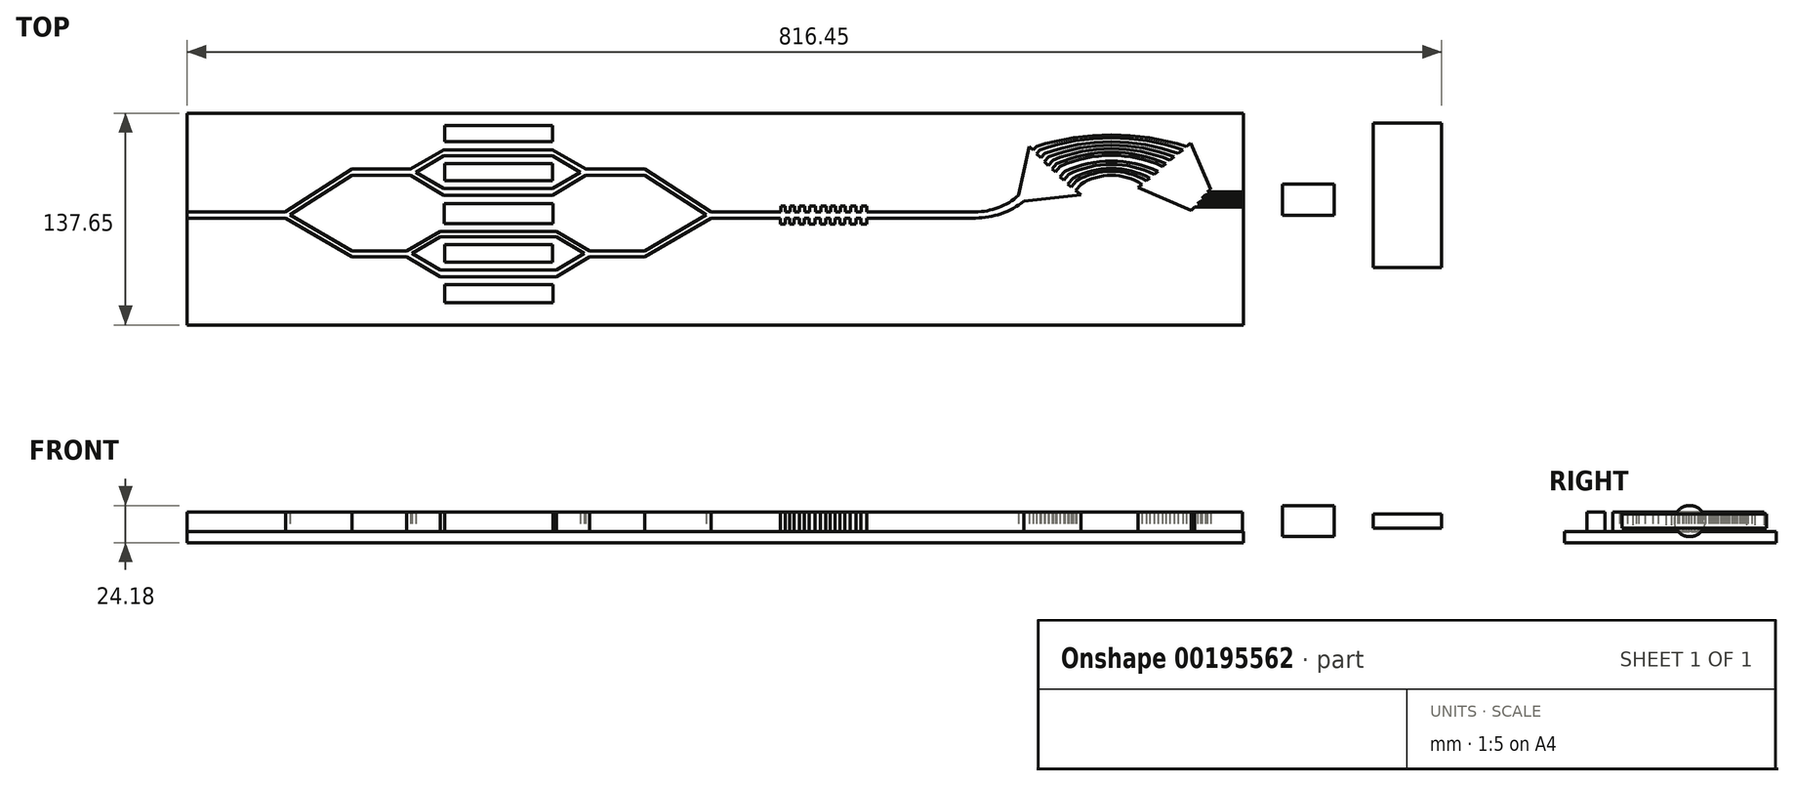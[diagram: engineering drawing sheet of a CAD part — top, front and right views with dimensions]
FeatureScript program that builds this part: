
annotation { "Feature Type Name" : "Feature", "Feature Type Description" : "" }
export const myFeature = defineFeature(function(context is Context, id is Id, definition is map)
    precondition{}
    {
        {
            var Q0;
            Q0=qCreatedBy(makeId("Top.planeOp"),FACE);
            var sketch = newSketch(context, id + "F0", { "sketchPlane" : qUnion([Q0])});
            skLineSegment(sketch, "E0.bottom", {"start": v(-202.47, -68.03) * mm, "end": v(484.95, -68.03) * mm});
            skLineSegment(sketch, "E0.top", {"start": v(-202.47, 69.62) * mm, "end": v(484.95, 69.62) * mm});
            skLineSegment(sketch, "E0.left", {"start": v(-202.47, -68.03) * mm, "end": v(-202.47, 69.62) * mm});
            skLineSegment(sketch, "E0.right", {"start": v(484.95, -68.03) * mm, "end": v(484.95, 69.62) * mm});
            skSolve(sketch);
        }
        {
            var Q0;
            Q0=qSketchRegion(id+"F0",true);
            extrude(context, id + "F1", {"entities" : qUnion([Q0]), "depth" : 7.37 * mm});
        }
        {
            var Q0;
            Q0=makeQuery(id+"F1.opExtrude","CAP_FACE",FACE,{"disambiguationData":[OSD([sQuery(id+"F0.wireOp",EDGE,"E0.bottom"),sQuery(id+"F0.wireOp",EDGE,"E0.top"),sQuery(id+"F0.wireOp",EDGE,"E0.left"),sQuery(id+"F0.wireOp",EDGE,"E0.right")])],"isStart":false});
            var sketch = newSketch(context, id + "F2", { "sketchPlane" : qUnion([Q0])});
            skLineSegment(sketch, "E1.bottom", {"start": v(-156.35, 5.45) * mm, "end": v(-138.65, 5.45) * mm});
            skLineSegment(sketch, "E1.top", {"start": v(-156.6, 1.4) * mm, "end": v(-138.42, 1.4) * mm});
            skLineSegment(sketch, "E2", {"start": v(-138.65, 5.45) * mm, "end": v(-95.28, 33.3) * mm});
            skLineSegment(sketch, "E3.MirrorCS", {"start": v(-138.42, 1.4) * mm, "end": v(-95.29, -23.79) * mm});
            skLineSegment(sketch, "E4", {"start": v(-95.29, 29.2) * mm, "end": v(-135.34, 3.48) * mm});
            skLineSegment(sketch, "E5", {"start": v(-95.29, -19.91) * mm, "end": v(-135.34, 3.48) * mm});
            skLineSegment(sketch, "E6", {"start": v(-95.28, 33.3) * mm, "end": v(-57.06, 33.3) * mm});
            skLineSegment(sketch, "E7", {"start": v(-95.29, 29.2) * mm, "end": v(-57.06, 29.2) * mm});
            skLineSegment(sketch, "E8", {"start": v(-95.29, -19.91) * mm, "end": v(-59.46, -19.91) * mm});
            skLineSegment(sketch, "E9", {"start": v(-95.29, -23.79) * mm, "end": v(-59.46, -23.79) * mm});
            skLineSegment(sketch, "E10", {"start": v(-57.06, 33.3) * mm, "end": v(-35.34, 45.95) * mm});
            skLineSegment(sketch, "E11", {"start": v(-57.06, 29.2) * mm, "end": v(-35.34, 16.28) * mm});
            skLineSegment(sketch, "E12", {"start": v(-53.49, 31.34) * mm, "end": v(-35.36, 42.1) * mm});
            skLineSegment(sketch, "E13", {"start": v(-53.49, 31.34) * mm, "end": v(-35.36, 20.57) * mm});
            skLineSegment(sketch, "E14", {"start": v(-59.46, -19.91) * mm, "end": v(-37.74, -7.26) * mm});
            skLineSegment(sketch, "E15", {"start": v(-59.46, -23.79) * mm, "end": v(-37.74, -36.71) * mm});
            skLineSegment(sketch, "E16", {"start": v(-55.94, -21.59) * mm, "end": v(-37.81, -10.82) * mm});
            skLineSegment(sketch, "E17", {"start": v(-55.94, -21.59) * mm, "end": v(-37.81, -32.35) * mm});
            skLineSegment(sketch, "E18", {"start": v(-35.34, 45.95) * mm, "end": v(0, 45.95) * mm});
            skLineSegment(sketch, "E19", {"start": v(-35.36, 42.1) * mm, "end": v(0, 42.1) * mm});
            skLineSegment(sketch, "E20", {"start": v(-35.36, 20.57) * mm, "end": v(0, 20.57) * mm});
            skLineSegment(sketch, "E21", {"start": v(-35.34, 16.28) * mm, "end": v(0, 16.28) * mm});
            skLineSegment(sketch, "E22", {"start": v(-37.74, -7.26) * mm, "end": v(0, -7.26) * mm});
            skLineSegment(sketch, "E23", {"start": v(-37.81, -10.82) * mm, "end": v(0, -10.82) * mm});
            skLineSegment(sketch, "E24", {"start": v(-37.81, -32.35) * mm, "end": v(0, -32.35) * mm});
            skLineSegment(sketch, "E25", {"start": v(-37.74, -36.71) * mm, "end": v(0, -36.71) * mm});
            skLineSegment(sketch, "E26.MirrorCS", {"start": v(95.29, -19.91) * mm, "end": v(135.34, 3.48) * mm});
            skLineSegment(sketch, "E27.MirrorCS", {"start": v(95.28, 33.3) * mm, "end": v(57.06, 33.3) * mm});
            skLineSegment(sketch, "E28.MirrorCS", {"start": v(95.29, 29.2) * mm, "end": v(135.34, 3.48) * mm});
            skLineSegment(sketch, "E29.MirrorCS", {"start": v(138.42, 1.4) * mm, "end": v(95.29, -23.79) * mm});
            skLineSegment(sketch, "E30.MirrorCS", {"start": v(37.74, -7.26) * mm, "end": v(0, -7.26) * mm});
            skLineSegment(sketch, "E31.MirrorCS", {"start": v(95.29, 29.2) * mm, "end": v(57.06, 29.2) * mm});
            skLineSegment(sketch, "E32.MirrorCS", {"start": v(95.29, -19.91) * mm, "end": v(59.46, -19.91) * mm});
            skLineSegment(sketch, "E33.MirrorCS", {"start": v(138.65, 5.45) * mm, "end": v(95.28, 33.3) * mm});
            skLineSegment(sketch, "E34.MirrorCS", {"start": v(55.94, -21.59) * mm, "end": v(37.81, -32.35) * mm});
            skLineSegment(sketch, "E35.MirrorCS", {"start": v(37.81, -10.82) * mm, "end": v(0, -10.82) * mm});
            skLineSegment(sketch, "E36.MirrorCS", {"start": v(53.49, 31.34) * mm, "end": v(35.36, 20.57) * mm});
            skLineSegment(sketch, "E37.MirrorCS", {"start": v(35.36, 42.1) * mm, "end": v(0, 42.1) * mm});
            skLineSegment(sketch, "E38.MirrorCS", {"start": v(35.34, 45.95) * mm, "end": v(0, 45.95) * mm});
            skLineSegment(sketch, "E39.MirrorCS", {"start": v(95.29, -23.79) * mm, "end": v(59.46, -23.79) * mm});
            skLineSegment(sketch, "E40.MirrorCS", {"start": v(55.94, -21.59) * mm, "end": v(37.81, -10.82) * mm});
            skLineSegment(sketch, "E41.MirrorCS", {"start": v(37.74, -36.71) * mm, "end": v(0, -36.71) * mm});
            skLineSegment(sketch, "E42.MirrorCS", {"start": v(59.46, -19.91) * mm, "end": v(37.74, -7.26) * mm});
            skLineSegment(sketch, "E43.MirrorCS", {"start": v(57.06, 33.3) * mm, "end": v(35.34, 45.95) * mm});
            skLineSegment(sketch, "E44.MirrorCS", {"start": v(35.36, 20.57) * mm, "end": v(0, 20.57) * mm});
            skLineSegment(sketch, "E45.MirrorCS", {"start": v(156.6, 1.4) * mm, "end": v(138.42, 1.4) * mm});
            skLineSegment(sketch, "E46.MirrorCS", {"start": v(57.06, 29.2) * mm, "end": v(35.34, 16.28) * mm});
            skLineSegment(sketch, "E47.MirrorCS", {"start": v(156.35, 5.45) * mm, "end": v(138.65, 5.45) * mm});
            skLineSegment(sketch, "E48.MirrorCS", {"start": v(59.46, -23.79) * mm, "end": v(37.74, -36.71) * mm});
            skLineSegment(sketch, "E49.MirrorCS", {"start": v(37.81, -32.35) * mm, "end": v(0, -32.35) * mm});
            skLineSegment(sketch, "E50.MirrorCS", {"start": v(35.34, 16.28) * mm, "end": v(0, 16.28) * mm});
            skLineSegment(sketch, "E51.MirrorCS", {"start": v(53.49, 31.34) * mm, "end": v(35.36, 42.1) * mm});
            skLineSegment(sketch, "E52", {"start": v(156.35, 5.45) * mm, "end": v(181.75, 5.45) * mm});
            skLineSegment(sketch, "E53", {"start": v(156.6, 1.4) * mm, "end": v(181.73, 1.4) * mm});
            skLineSegment(sketch, "E54", {"start": v(183.86, 5.45) * mm, "end": v(183.86, 9.35) * mm});
            skLineSegment(sketch, "E55", {"start": v(183.86, 9.35) * mm, "end": v(186.92, 9.35) * mm});
            skLineSegment(sketch, "E56", {"start": v(186.92, 9.35) * mm, "end": v(186.92, 5.6) * mm});
            skLineSegment(sketch, "E57", {"start": v(186.92, 5.6) * mm, "end": v(189.9, 5.6) * mm});
            skLineSegment(sketch, "E58", {"start": v(189.9, 5.6) * mm, "end": v(189.9, 9.35) * mm});
            skLineSegment(sketch, "E59", {"start": v(189.9, 9.35) * mm, "end": v(192.9, 9.35) * mm});
            skLineSegment(sketch, "E60", {"start": v(192.9, 9.35) * mm, "end": v(192.9, 5.6) * mm});
            skLineSegment(sketch, "E61", {"start": v(192.9, 5.6) * mm, "end": v(196.13, 5.6) * mm});
            skLineSegment(sketch, "E62", {"start": v(196.13, 5.6) * mm, "end": v(196.13, 9.35) * mm});
            skLineSegment(sketch, "E63", {"start": v(196.13, 9.35) * mm, "end": v(199.35, 9.35) * mm});
            skLineSegment(sketch, "E64", {"start": v(199.35, 9.35) * mm, "end": v(199.35, 5.6) * mm});
            skLineSegment(sketch, "E65", {"start": v(199.35, 5.6) * mm, "end": v(202.73, 5.6) * mm});
            skLineSegment(sketch, "E66", {"start": v(202.73, 5.6) * mm, "end": v(202.73, 9.35) * mm});
            skLineSegment(sketch, "E67", {"start": v(202.73, 9.35) * mm, "end": v(206.5, 9.35) * mm});
            skLineSegment(sketch, "E68", {"start": v(206.5, 9.35) * mm, "end": v(206.5, 5.6) * mm});
            skLineSegment(sketch, "E69", {"start": v(206.5, 5.6) * mm, "end": v(209.87, 5.6) * mm});
            skLineSegment(sketch, "E70", {"start": v(209.87, 5.6) * mm, "end": v(209.87, 9.35) * mm});
            skLineSegment(sketch, "E71", {"start": v(209.87, 9.35) * mm, "end": v(213.4, 9.35) * mm});
            skLineSegment(sketch, "E72", {"start": v(213.4, 9.35) * mm, "end": v(213.4, 5.6) * mm});
            skLineSegment(sketch, "E73.MirrorCS", {"start": v(186.66, -2.29) * mm, "end": v(186.66, 1.48) * mm});
            skLineSegment(sketch, "E74.MirrorCS", {"start": v(199.1, 1.48) * mm, "end": v(202.48, 1.48) * mm});
            skLineSegment(sketch, "E75.MirrorCS", {"start": v(199.1, -2.29) * mm, "end": v(199.1, 1.48) * mm});
            skLineSegment(sketch, "E76.MirrorCS", {"start": v(189.66, 1.48) * mm, "end": v(189.66, -2.29) * mm});
            skLineSegment(sketch, "E77.MirrorCS", {"start": v(186.66, 1.48) * mm, "end": v(189.66, 1.48) * mm});
            skLineSegment(sketch, "E78.MirrorCS", {"start": v(202.48, 1.48) * mm, "end": v(202.48, -2.29) * mm});
            skLineSegment(sketch, "E79.MirrorCS", {"start": v(189.66, -2.29) * mm, "end": v(192.65, -2.29) * mm});
            skLineSegment(sketch, "E80.MirrorCS", {"start": v(202.48, -2.29) * mm, "end": v(206.24, -2.29) * mm});
            skLineSegment(sketch, "E81.MirrorCS", {"start": v(192.65, -2.29) * mm, "end": v(192.65, 1.48) * mm});
            skLineSegment(sketch, "E82.MirrorCS", {"start": v(192.65, 1.48) * mm, "end": v(195.87, 1.48) * mm});
            skLineSegment(sketch, "E83.MirrorCS", {"start": v(206.24, -2.29) * mm, "end": v(206.24, 1.48) * mm});
            skLineSegment(sketch, "E84.MirrorCS", {"start": v(195.87, 1.48) * mm, "end": v(195.87, -2.29) * mm});
            skLineSegment(sketch, "E85.MirrorCS", {"start": v(183.6, -2.29) * mm, "end": v(186.66, -2.29) * mm});
            skLineSegment(sketch, "E86.MirrorCS", {"start": v(206.24, 1.48) * mm, "end": v(209.62, 1.48) * mm});
            skLineSegment(sketch, "E87.MirrorCS", {"start": v(209.62, 1.48) * mm, "end": v(209.62, -2.29) * mm});
            skLineSegment(sketch, "E88.MirrorCS", {"start": v(195.87, -2.29) * mm, "end": v(199.1, -2.29) * mm});
            skLineSegment(sketch, "E89.MirrorCS", {"start": v(209.62, -2.29) * mm, "end": v(213.15, -2.29) * mm});
            skLineSegment(sketch, "E90.MirrorCS", {"start": v(183.61, 1.4) * mm, "end": v(183.6, -2.29) * mm});
            skLineSegment(sketch, "E91.MirrorCS", {"start": v(213.15, -2.29) * mm, "end": v(213.15, 1.48) * mm});
            skLineSegment(sketch, "E92", {"start": v(213.4, 5.6) * mm, "end": v(216.4, 5.6) * mm});
            skLineSegment(sketch, "E93", {"start": v(216.4, 5.6) * mm, "end": v(216.4, 9.35) * mm});
            skLineSegment(sketch, "E94", {"start": v(216.4, 9.35) * mm, "end": v(219.39, 9.35) * mm});
            skLineSegment(sketch, "E95", {"start": v(219.39, 9.35) * mm, "end": v(219.39, 5.6) * mm});
            skLineSegment(sketch, "E96", {"start": v(219.39, 5.6) * mm, "end": v(222.61, 5.6) * mm});
            skLineSegment(sketch, "E97", {"start": v(222.61, 5.6) * mm, "end": v(222.61, 9.35) * mm});
            skLineSegment(sketch, "E98", {"start": v(222.61, 9.35) * mm, "end": v(225.84, 9.35) * mm});
            skLineSegment(sketch, "E99", {"start": v(225.84, 9.35) * mm, "end": v(225.84, 5.6) * mm});
            skLineSegment(sketch, "E100", {"start": v(225.84, 5.6) * mm, "end": v(229.22, 5.6) * mm});
            skLineSegment(sketch, "E101", {"start": v(229.22, 5.6) * mm, "end": v(229.22, 9.35) * mm});
            skLineSegment(sketch, "E102", {"start": v(229.22, 9.35) * mm, "end": v(232.98, 9.35) * mm});
            skLineSegment(sketch, "E103", {"start": v(232.98, 9.35) * mm, "end": v(232.98, 5.6) * mm});
            skLineSegment(sketch, "E104", {"start": v(232.98, 5.6) * mm, "end": v(236.36, 5.6) * mm});
            skLineSegment(sketch, "E105", {"start": v(236.36, 5.6) * mm, "end": v(236.36, 9.35) * mm});
            skLineSegment(sketch, "E106", {"start": v(236.36, 9.35) * mm, "end": v(239.89, 9.35) * mm});
            skLineSegment(sketch, "E107", {"start": v(239.89, 9.35) * mm, "end": v(239.89, 5.5) * mm});
            skLineSegment(sketch, "E108.MirrorCS", {"start": v(225.58, 1.48) * mm, "end": v(228.96, 1.48) * mm});
            skLineSegment(sketch, "E109.MirrorCS", {"start": v(225.58, -2.29) * mm, "end": v(225.58, 1.48) * mm});
            skLineSegment(sketch, "E110.MirrorCS", {"start": v(216.14, 1.48) * mm, "end": v(216.14, -2.29) * mm});
            skLineSegment(sketch, "E111.MirrorCS", {"start": v(213.15, 1.48) * mm, "end": v(216.14, 1.48) * mm});
            skLineSegment(sketch, "E112.MirrorCS", {"start": v(228.96, 1.48) * mm, "end": v(228.96, -2.29) * mm});
            skLineSegment(sketch, "E113.MirrorCS", {"start": v(216.14, -2.29) * mm, "end": v(219.14, -2.29) * mm});
            skLineSegment(sketch, "E114.MirrorCS", {"start": v(228.96, -2.29) * mm, "end": v(232.72, -2.29) * mm});
            skLineSegment(sketch, "E115.MirrorCS", {"start": v(219.14, -2.29) * mm, "end": v(219.14, 1.48) * mm});
            skLineSegment(sketch, "E116.MirrorCS", {"start": v(219.14, 1.48) * mm, "end": v(222.36, 1.48) * mm});
            skLineSegment(sketch, "E117.MirrorCS", {"start": v(232.72, -2.29) * mm, "end": v(232.72, 1.48) * mm});
            skLineSegment(sketch, "E118.MirrorCS", {"start": v(222.36, 1.48) * mm, "end": v(222.36, -2.29) * mm});
            skLineSegment(sketch, "E119.MirrorCS", {"start": v(232.72, 1.48) * mm, "end": v(236.1, 1.48) * mm});
            skLineSegment(sketch, "E120.MirrorCS", {"start": v(236.1, 1.48) * mm, "end": v(236.1, -2.29) * mm});
            skLineSegment(sketch, "E121.MirrorCS", {"start": v(222.36, -2.29) * mm, "end": v(225.58, -2.29) * mm});
            skLineSegment(sketch, "E122.MirrorCS", {"start": v(236.1, -2.29) * mm, "end": v(239.89, -2.29) * mm});
            skLineSegment(sketch, "E123.MirrorCS", {"start": v(239.89, -2.29) * mm, "end": v(239.89, 1.52) * mm});
            skLineSegment(sketch, "E124", {"start": v(183.86, 5.45) * mm, "end": v(181.75, 5.45) * mm});
            skLineSegment(sketch, "E125", {"start": v(183.61, 1.4) * mm, "end": v(181.73, 1.4) * mm});
            skLineSegment(sketch, "E126", {"start": v(-156.35, 5.45) * mm, "end": v(-202.47, 5.45) * mm});
            skLineSegment(sketch, "E127", {"start": v(-156.6, 1.4) * mm, "end": v(-202.47, 1.4) * mm});
            skLineSegment(sketch, "E128", {"start": v(-202.47, 1.4) * mm, "end": v(-202.47, 5.45) * mm});
            skLineSegment(sketch, "E129.bottom", {"start": v(-34.86, 37.06) * mm, "end": v(35.38, 37.06) * mm});
            skLineSegment(sketch, "E129.top", {"start": v(-34.86, 25.76) * mm, "end": v(35.38, 25.76) * mm});
            skLineSegment(sketch, "E129.left", {"start": v(-34.86, 37.06) * mm, "end": v(-34.86, 25.76) * mm});
            skLineSegment(sketch, "E129.right", {"start": v(35.38, 37.06) * mm, "end": v(35.38, 25.76) * mm});
            skLineSegment(sketch, "E130.bottom", {"start": v(-34.88, -15.89) * mm, "end": v(35.37, -15.89) * mm});
            skLineSegment(sketch, "E130.top", {"start": v(-34.88, -27.19) * mm, "end": v(35.37, -27.19) * mm});
            skLineSegment(sketch, "E130.left", {"start": v(-34.88, -15.89) * mm, "end": v(-34.88, -27.19) * mm});
            skLineSegment(sketch, "E130.right", {"start": v(35.37, -15.89) * mm, "end": v(35.37, -27.19) * mm});
            skLineSegment(sketch, "E131.bottom", {"start": v(-34.82, 61.76) * mm, "end": v(35.43, 61.76) * mm});
            skLineSegment(sketch, "E131.top", {"start": v(-34.82, 51.34) * mm, "end": v(35.43, 51.34) * mm});
            skLineSegment(sketch, "E131.left", {"start": v(-34.82, 61.76) * mm, "end": v(-34.82, 51.34) * mm});
            skLineSegment(sketch, "E131.right", {"start": v(35.43, 61.76) * mm, "end": v(35.43, 51.34) * mm});
            skLineSegment(sketch, "E132.bottom", {"start": v(-35.26, 11.01) * mm, "end": v(35.65, 11.01) * mm});
            skLineSegment(sketch, "E132.top", {"start": v(-35.26, -2.06) * mm, "end": v(35.65, -2.06) * mm});
            skLineSegment(sketch, "E132.left", {"start": v(-35.26, 11.01) * mm, "end": v(-35.26, -2.06) * mm});
            skLineSegment(sketch, "E132.right", {"start": v(35.65, 11.01) * mm, "end": v(35.65, -2.06) * mm});
            skLineSegment(sketch, "E133.bottom", {"start": v(-34.82, -41.73) * mm, "end": v(35.65, -41.73) * mm});
            skLineSegment(sketch, "E133.top", {"start": v(-34.82, -53.47) * mm, "end": v(35.65, -53.47) * mm});
            skLineSegment(sketch, "E133.left", {"start": v(-34.82, -41.73) * mm, "end": v(-34.82, -53.47) * mm});
            skLineSegment(sketch, "E133.right", {"start": v(35.65, -41.73) * mm, "end": v(35.65, -53.47) * mm});
            skLineSegment(sketch, "E134", {"start": v(239.89, 5.5) * mm, "end": v(247.4, 5.5) * mm});
            skLineSegment(sketch, "E135", {"start": v(247.4, 1.52) * mm, "end": v(239.89, 1.52) * mm});
            skLineSegment(sketch, "E136", {"start": v(247.4, 5.5) * mm, "end": v(310.4, 5.5) * mm});
            skArc(sketch, "E137", {"start": v(310.4, 5.5) * mm, "mid": v(325.49, 8.3) * mm, "end": v(338.58, 16.28) * mm});
            skLineSegment(sketch, "E138", {"start": v(247.4, 1.52) * mm, "end": v(310.57, 1.52) * mm});
            skArc(sketch, "E139", {"start": v(310.57, 1.52) * mm, "mid": v(327.26, 4.37) * mm, "end": v(342.1, 12.52) * mm});
            skLineSegment(sketch, "E140", {"start": v(338.58, 16.28) * mm, "end": v(345.62, 48.01) * mm});
            skLineSegment(sketch, "E141", {"start": v(345.62, 48.01) * mm, "end": v(348.2, 45.76) * mm});
            skLineSegment(sketch, "E142", {"start": v(348.2, 45.76) * mm, "end": v(350.17, 48.01) * mm});
            skLineSegment(sketch, "E143", {"start": v(352.55, 45.93) * mm, "end": v(350.17, 43.2) * mm});
            skLineSegment(sketch, "E144", {"start": v(350.17, 43.2) * mm, "end": v(353.08, 40.66) * mm});
            skLineSegment(sketch, "E145", {"start": v(353.08, 40.66) * mm, "end": v(355.57, 43.5) * mm});
            skLineSegment(sketch, "E146", {"start": v(358.09, 41.3) * mm, "end": v(355.33, 38.15) * mm});
            skLineSegment(sketch, "E147", {"start": v(355.33, 38.15) * mm, "end": v(358.04, 35.78) * mm});
            skLineSegment(sketch, "E148", {"start": v(358.04, 35.78) * mm, "end": v(361.02, 39.19) * mm});
            skLineSegment(sketch, "E149", {"start": v(363.44, 36.92) * mm, "end": v(360.48, 33.54) * mm});
            skLineSegment(sketch, "E150", {"start": v(360.48, 33.54) * mm, "end": v(362.63, 31.66) * mm});
            skLineSegment(sketch, "E151", {"start": v(362.63, 31.66) * mm, "end": v(365.64, 35.1) * mm});
            skLineSegment(sketch, "E152", {"start": v(368.63, 31.74) * mm, "end": v(365.64, 28.32) * mm});
            skLineSegment(sketch, "E153", {"start": v(365.64, 28.32) * mm, "end": v(368.06, 26.2) * mm});
            skLineSegment(sketch, "E154", {"start": v(368.06, 26.2) * mm, "end": v(371.28, 29.87) * mm});
            skLineSegment(sketch, "E155", {"start": v(374.05, 27.44) * mm, "end": v(370.64, 23.53) * mm});
            skLineSegment(sketch, "E156", {"start": v(370.64, 23.53) * mm, "end": v(372.72, 21.7) * mm});
            skLineSegment(sketch, "E157", {"start": v(372.72, 21.7) * mm, "end": v(376.3, 25.8) * mm});
            skLineSegment(sketch, "E158", {"start": v(379.04, 23.42) * mm, "end": v(375.7, 19.6) * mm});
            skLineSegment(sketch, "E159", {"start": v(375.7, 19.6) * mm, "end": v(379.04, 16.68) * mm});
            skLineSegment(sketch, "E160", {"start": v(379.04, 16.68) * mm, "end": v(342.1, 12.52) * mm});
            skArc(sketch, "E161", {"start": v(379.04, 23.42) * mm, "mid": v(399, 29.22) * mm, "end": v(418.98, 23.42) * mm});
            skArc(sketch, "E162", {"start": v(376.3, 25.8) * mm, "mid": v(399, 31.93) * mm, "end": v(421.7, 25.8) * mm});
            skArc(sketch, "E163", {"start": v(374.05, 27.44) * mm, "mid": v(399, 33.78) * mm, "end": v(423.96, 27.44) * mm});
            skArc(sketch, "E164", {"start": v(371.28, 29.87) * mm, "mid": v(399, 36.4) * mm, "end": v(426.74, 29.87) * mm});
            skArc(sketch, "E165", {"start": v(368.63, 31.74) * mm, "mid": v(399, 38.53) * mm, "end": v(429.38, 31.74) * mm});
            skArc(sketch, "E166", {"start": v(365.64, 35.1) * mm, "mid": v(399, 42.27) * mm, "end": v(432.38, 35.1) * mm});
            skArc(sketch, "E167", {"start": v(363.44, 36.92) * mm, "mid": v(399, 44.28) * mm, "end": v(434.58, 36.92) * mm});
            skArc(sketch, "E168", {"start": v(361.02, 39.19) * mm, "mid": v(399, 46.64) * mm, "end": v(437, 39.19) * mm});
            skArc(sketch, "E169", {"start": v(358.09, 41.3) * mm, "mid": v(399, 48.93) * mm, "end": v(439.93, 41.3) * mm});
            skArc(sketch, "E170", {"start": v(355.57, 43.5) * mm, "mid": v(399, 51.1) * mm, "end": v(442.44, 43.5) * mm});
            skArc(sketch, "E171", {"start": v(352.55, 45.93) * mm, "mid": v(399, 53.68) * mm, "end": v(445.47, 45.93) * mm});
            skArc(sketch, "E172", {"start": v(350.17, 48.01) * mm, "mid": v(399, 55.56) * mm, "end": v(447.85, 48.01) * mm});
            skLineSegment(sketch, "E173", {"start": v(421.7, 25.8) * mm, "end": v(423.96, 27.44) * mm});
            skLineSegment(sketch, "E174", {"start": v(426.74, 29.87) * mm, "end": v(429.38, 31.74) * mm});
            skLineSegment(sketch, "E175", {"start": v(432.38, 35.1) * mm, "end": v(434.58, 36.92) * mm});
            skLineSegment(sketch, "E176", {"start": v(437, 39.19) * mm, "end": v(439.93, 41.3) * mm});
            skLineSegment(sketch, "E177", {"start": v(442.44, 43.5) * mm, "end": v(445.47, 45.93) * mm});
            skLineSegment(sketch, "E178", {"start": v(418.98, 23.42) * mm, "end": v(416.37, 21.29) * mm});
            skLineSegment(sketch, "E179", {"start": v(416.37, 21.29) * mm, "end": v(450.94, 6.45) * mm});
            skLineSegment(sketch, "E180", {"start": v(447.85, 48.01) * mm, "end": v(450.59, 50.33) * mm});
            skLineSegment(sketch, "E181", {"start": v(450.59, 50.33) * mm, "end": v(463.67, 20.17) * mm});
            skLineSegment(sketch, "E182", {"start": v(463.67, 20.17) * mm, "end": v(461.3, 18.35) * mm});
            skLineSegment(sketch, "E183", {"start": v(461.3, 18.35) * mm, "end": v(484.43, 18.35) * mm});
            skLineSegment(sketch, "E184", {"start": v(460.04, 16.54) * mm, "end": v(484.43, 16.54) * mm});
            skLineSegment(sketch, "E185", {"start": v(450.94, 6.45) * mm, "end": v(453.3, 8.59) * mm});
            skLineSegment(sketch, "E186", {"start": v(453.3, 8.59) * mm, "end": v(484.43, 8.59) * mm});
            skLineSegment(sketch, "E187", {"start": v(455, 10.82) * mm, "end": v(484.43, 10.82) * mm});
            skLineSegment(sketch, "E188", {"start": v(457.05, 12.63) * mm, "end": v(484.43, 12.63) * mm});
            skLineSegment(sketch, "E189", {"start": v(457.95, 14.45) * mm, "end": v(484.43, 14.45) * mm});
            skLineSegment(sketch, "E190", {"start": v(457.95, 14.45) * mm, "end": v(460.04, 16.54) * mm});
            skLineSegment(sketch, "E191", {"start": v(457.05, 12.63) * mm, "end": v(455, 10.82) * mm});
            skLineSegment(sketch, "E192", {"start": v(484.43, 18.35) * mm, "end": v(484.43, 16.54) * mm});
            skLineSegment(sketch, "E193", {"start": v(484.43, 14.45) * mm, "end": v(484.43, 12.63) * mm});
            skLineSegment(sketch, "E194", {"start": v(484.43, 10.82) * mm, "end": v(484.43, 8.59) * mm});
            skSolve(sketch);
        }
        {
            var Q0;
            Q0=qSketchRegion(id+"F2",true);
            var Q1;
            Q1=makeQuery(id+"F2.imprint","IMPRINT",FACE,{"disambiguationData":[TD([[makeQuery(id+"F2.imprint","IMPRINT",EDGE,{"derivedFrom":sQuery(id+"F2.wireOp",EDGE,"E129.bottom")}),-1.0]])]});
            var Q2;
            Q2=makeQuery(id+"F2.imprint","IMPRINT",FACE,{"disambiguationData":[TD([[makeQuery(id+"F2.imprint","IMPRINT",EDGE,{"derivedFrom":sQuery(id+"F2.wireOp",EDGE,"E132.bottom")}),-1.0]])]});
            var Q3;
            Q3=makeQuery(id+"F2.imprint","IMPRINT",FACE,{"disambiguationData":[TD([[makeQuery(id+"F2.imprint","IMPRINT",EDGE,{"derivedFrom":sQuery(id+"F2.wireOp",EDGE,"E130.bottom")}),-1.0]])]});
            extrude(context, id + "F3", {"entities" : qUnion([Q0, Q1, Q2, Q3]), "operationType" : NewBodyOperationType.ADD, "depth" : 12.45 * mm});
        }
        {
            var Q0;
            Q0=makeQuery(id+"F1.opExtrude","SWEPT_FACE",FACE,{"disambiguationData":[OSD([sQuery(id+"F0.wireOp",EDGE,"E0.right")])]});
            cPlane(context, id + "F4", {"entities" : qUnion([Q0]), "cplaneType" : CPlaneType.OFFSET, "offset" : 25.4 * mm, "width" : 152.4 * mm, "height" : 152.4 * mm});
        }
        {
            var Q0;
            Q0=qCreatedBy(id+"F4.planeOp",FACE);
            var sketch = newSketch(context, id + "F5", { "sketchPlane" : qUnion([Q0])});
            skCircle(sketch, "E195", {"center": v(13.34, 14.05) * mm, "radius": 10.12 * mm});
            skSolve(sketch);
        }
        {
            var Q0;
            Q0 = qSketchRegion(id + "F5", true);
            extrude(context, id + "F6", {"entities" : qUnion([Q0]), "depth" : 33.78 * mm});
        }
        {
            var Q0;
            Q0=makeQuery(id+"F6.opExtrude","CAP_FACE",FACE,{"disambiguationData":[OSD([sQuery(id+"F5.wireOp",EDGE,"E195")])],"isStart":false});
            cPlane(context, id + "F7", {"entities" : qUnion([Q0]), "cplaneType" : CPlaneType.OFFSET, "offset" : 25.4 * mm, "width" : 152.4 * mm, "height" : 152.4 * mm});
        }
        {
            var Q0;
            Q0=qCreatedBy(id+"F7.planeOp",FACE);
            var sketch = newSketch(context, id + "F8", { "sketchPlane" : qUnion([Q0])});
            skLineSegment(sketch, "E196.bottom", {"start": v(-30.65, 18.72) * mm, "end": v(63.2, 18.72) * mm});
            skLineSegment(sketch, "E196.top", {"start": v(-30.65, 9.44) * mm, "end": v(63.2, 9.44) * mm});
            skLineSegment(sketch, "E196.left", {"start": v(-30.65, 18.72) * mm, "end": v(-30.65, 9.44) * mm});
            skLineSegment(sketch, "E196.right", {"start": v(63.2, 18.72) * mm, "end": v(63.2, 9.44) * mm});
            skSolve(sketch);
        }
        {
            var Q0;
            Q0 = qSketchRegion(id + "F8", true);
            extrude(context, id + "F9", {"entities" : qUnion([Q0]), "depth" : 44.45 * mm});
        }
    });
